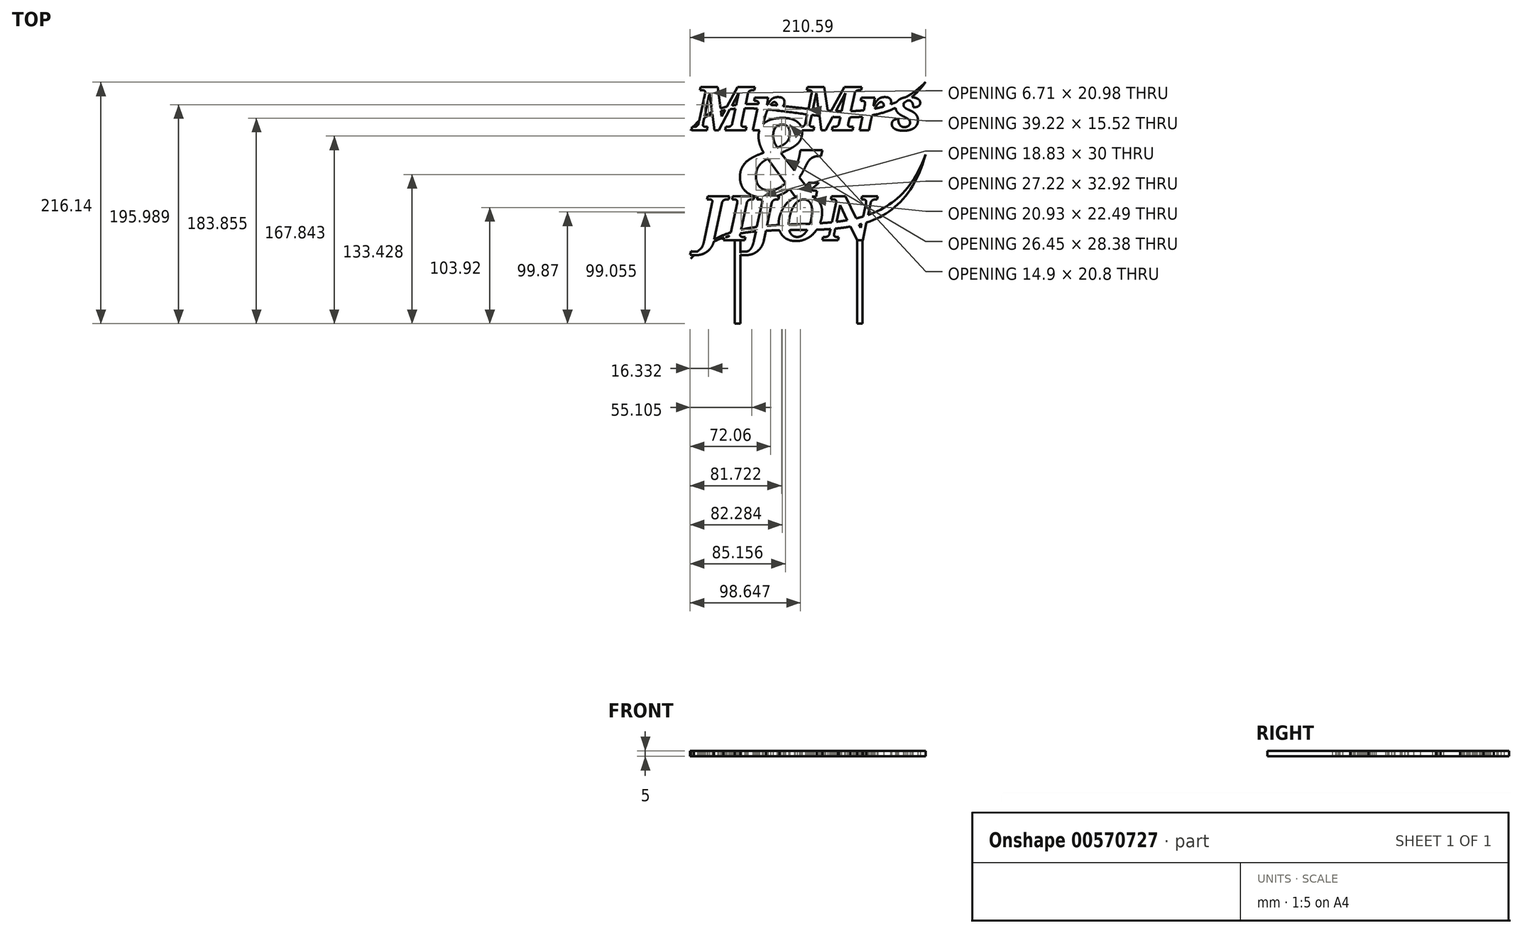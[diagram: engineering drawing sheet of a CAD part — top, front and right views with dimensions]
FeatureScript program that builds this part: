
annotation { "Feature Type Name" : "Feature", "Feature Type Description" : "" }
export const myFeature = defineFeature(function(context is Context, id is Id, definition is map)
    precondition{}
    {
        {
            var Q0;
            Q0=qCreatedBy(makeId("Top.planeOp"),FACE);
            var sketch = newSketch(context, id + "F0", { "sketchPlane" : qUnion([Q0])});
            skText(sketch, "E0", { "text": "Mr Mrs", "fontName": "NotoSerif-BoldItalic.ttf"});
            skText(sketch, "E1", { "text": "JIJÓN", "fontName": "NotoSerif-BoldItalic.ttf"});
            skText(sketch, "E2", { "text": "&", "fontName": "NotoSerif-BoldItalic.ttf"});
            skLineSegment(sketch, "E3.bottom", {"start": v(-105, -105) * mm, "end": v(105, -105) * mm, "construction": true});
            skLineSegment(sketch, "E3.top", {"start": v(-105, 105) * mm, "end": v(105, 105) * mm, "construction": true});
            skLineSegment(sketch, "E3.left", {"start": v(-105, -105) * mm, "end": v(-105, 105) * mm, "construction": true});
            skLineSegment(sketch, "E3.right", {"start": v(105, -105) * mm, "end": v(105, 105) * mm, "construction": true});
            skPoint(sketch, "E3.middle", {"position": v(0, 0) * mm});
            skPoint(sketch, "E4.1.internal.snap0", {"position": v(-96.8, -28.16) * mm});
            skFitSpline(sketch, "E5", {"points": [v(-105, -64.5) * mm, v(105, 28.69) * mm], "startDerivative": vector(161.97, 193.53) * mm, "endDerivative": vector(112.25, 314.45) * mm});
            skFitSpline(sketch, "E6", {"points": [v(-105, -64.5) * mm, v(105, 28.69) * mm], "startDerivative": vector(161.97, 179.42) * mm, "endDerivative": vector(95.19, 344.92) * mm});
            skFitSpline(sketch, "E7", {"points": [v(-105, 50.55) * mm, v(105, 93.54) * mm], "startDerivative": vector(127.56, 176.19) * mm, "endDerivative": vector(187.71, 188.88) * mm});
            skFitSpline(sketch, "E8", {"points": [v(-105, 50.55) * mm, v(105, 93.54) * mm], "startDerivative": vector(127.56, 163.36) * mm, "endDerivative": vector(158.48, 219.65) * mm});
            skLineSegment(sketch, "E9.bottom", {"start": v(-60.68, -48.16) * mm, "end": v(-65.68, -48.16) * mm});
            skLineSegment(sketch, "E9.top", {"start": v(-60.68, -122.6) * mm, "end": v(-65.68, -122.6) * mm});
            skLineSegment(sketch, "E9.left", {"start": v(-60.68, -48.16) * mm, "end": v(-60.68, -122.6) * mm});
            skLineSegment(sketch, "E9.right", {"start": v(-65.68, -48.16) * mm, "end": v(-65.68, -122.6) * mm});
            skLineSegment(sketch, "E10.bottom", {"start": v(43.74, -48.16) * mm, "end": v(48.74, -48.16) * mm});
            skLineSegment(sketch, "E10.top", {"start": v(43.74, -122.6) * mm, "end": v(48.74, -122.6) * mm});
            skLineSegment(sketch, "E10.left", {"start": v(43.74, -48.16) * mm, "end": v(43.74, -122.6) * mm});
            skLineSegment(sketch, "E10.right", {"start": v(48.74, -48.16) * mm, "end": v(48.74, -122.6) * mm});
            skPoint(sketch, "E11", {"position": v(105, 70.05) * mm});
            const initialGuessF0  = {"E0": [-0.10303, 0.05055, 1, 0, 0.039], "E1": [-0.0968, -0.04816, 1, 0, 0.04], "E2": [-0.06436, -0.00892, 1, 0, 0.07]};
            skSetInitialGuess(sketch, initialGuessF0);
            skSolve(sketch);
        }
        {
            var Q0;
            {var subQ0=sQuery(id+"F0.wireOp",EDGE,"E6");var subQ1=sQuery(id+"F0.wireOp",EDGE,"E1.sketch_text.stroke-95");var subQ2=makeQuery(id+"F0.imprint","INTERSECT",VERTEX,{"derivedFrom":[subQ1,subQ0]});var subQ3=sQuery(id+"F0.wireOp",EDGE,"E5");var subQ5=makeQuery(id+"F0.imprint","IMPRINT",EDGE,{"disambiguationData":[TD([[subQ2,1.0]])],"derivedFrom":subQ1});var subQ6=sQuery(id+"F0.wireOp",EDGE,"E1.sketch_text.stroke-115");var subQ7=makeQuery(id+"F0.imprint","INTERSECT",VERTEX,{"derivedFrom":[subQ6,subQ0]});var subQ9=makeQuery(id+"F0.imprint","IMPRINT",EDGE,{"disambiguationData":[TD([[subQ7,-1.0]])],"derivedFrom":subQ6});var subQ13=sQuery(id+"F0.wireOp",EDGE,"E1.sketch_text.stroke-37");var subQ20=makeQuery(id+"F0.imprint","IMPRINT",EDGE,{"derivedFrom":subQ13});var subQ23=sQuery(id+"F0.wireOp",EDGE,"E1.sketch_text.stroke-192");var subQ24=makeQuery(id+"F0.imprint","INTERSECT",VERTEX,{"derivedFrom":[subQ23,subQ0]});var subQ26=makeQuery(id+"F0.imprint","IMPRINT",EDGE,{"disambiguationData":[TD([[subQ24,1.0]])],"derivedFrom":subQ23});var subQ37=sQuery(id+"F0.wireOp",EDGE,"E1.sketch_text.stroke-107");var subQ40=sQuery(id+"F0.wireOp",EDGE,"E1.sketch_text.stroke-96");var subQ48=sQuery(id+"F0.wireOp",EDGE,"E0.sketch_text.stroke-152");var subQ50=sQuery(id+"F0.wireOp",EDGE,"E7");var subQ56=makeQuery(id+"F0.imprint","IMPRINT",EDGE,{"derivedFrom":subQ48});var subQ58=sQuery(id+"F0.wireOp",EDGE,"E8");var subQ59=sQuery(id+"F0.wireOp",EDGE,"E0.sketch_text.stroke-51");var subQ60=makeQuery(id+"F0.imprint","INTERSECT",VERTEX,{"derivedFrom":[subQ59,subQ58]});var subQ63=sQuery(id+"F0.wireOp",EDGE,"E0.sketch_text.stroke-24");var subQ64=sQuery(id+"F0.wireOp",EDGE,"E0.sketch_text.stroke-23");var subQ65=makeQuery(id+"F0.imprint","INTERSECT",VERTEX,{"derivedFrom":[subQ64,subQ58]});var subQ68=sQuery(id+"F0.wireOp",EDGE,"E0.sketch_text.stroke-25");var subQ75=sQuery(id+"F0.wireOp",EDGE,"E1.sketch_text.stroke-109");var subQ76=sQuery(id+"F0.wireOp",EDGE,"E1.sketch_text.stroke-108");var subQ84=sQuery(id+"F0.wireOp",EDGE,"E1.sketch_text.stroke-193");var subQ89=sQuery(id+"F0.wireOp",EDGE,"E0.sketch_text.stroke-82");var subQ106=sQuery(id+"F0.wireOp",EDGE,"E0.sketch_text.stroke-60");var subQ108=makeQuery(id+"F0.imprint","IMPRINT",EDGE,{"derivedFrom":subQ89});var subQ109=makeQuery(id+"F0.imprint","IMPRINT",EDGE,{"derivedFrom":subQ106});var subQ115=makeQuery(id+"F0.imprint","INTERSECT",VERTEX,{"derivedFrom":[subQ68,subQ50]});var subQ116=sQuery(id+"F0.wireOp",EDGE,"E0.sketch_text.stroke-26");var subQ120=sQuery(id+"F0.wireOp",EDGE,"E0.sketch_text.stroke-43");var subQ126=sQuery(id+"F0.wireOp",EDGE,"E1.sketch_text.stroke-151");var subQ127=sQuery(id+"F0.wireOp",EDGE,"E1.sketch_text.stroke-150");var subQ130=makeQuery(id+"F0.imprint","INTERSECT",VERTEX,{"derivedFrom":[subQ127,subQ3]});var subQ133=sQuery(id+"F0.wireOp",EDGE,"E1.sketch_text.stroke-168");var subQ135=sQuery(id+"F0.wireOp",EDGE,"E1.sketch_text.stroke-176");var subQ136=makeQuery(id+"F0.imprint","INTERSECT",VERTEX,{"derivedFrom":[subQ135,subQ3]});var subQ139=sQuery(id+"F0.wireOp",EDGE,"E0.sketch_text.stroke-106");var subQ140=makeQuery(id+"F0.imprint","INTERSECT",VERTEX,{"derivedFrom":[subQ139,subQ50]});var subQ142=makeQuery(id+"F0.imprint","IMPRINT",EDGE,{"disambiguationData":[TD([[subQ140,1.0]])],"derivedFrom":subQ139});var subQ143=sQuery(id+"F0.wireOp",EDGE,"E0.sketch_text.stroke-107");var subQ144=makeQuery(id+"F0.imprint","INTERSECT",VERTEX,{"derivedFrom":[subQ143,subQ58]});var subQ146=makeQuery(id+"F0.imprint","IMPRINT",EDGE,{"disambiguationData":[TD([[subQ144,1.0]])],"derivedFrom":subQ143});var subQ147=sQuery(id+"F0.wireOp",EDGE,"E0.sketch_text.stroke-136");var subQ148=sQuery(id+"F0.wireOp",EDGE,"E0.sketch_text.stroke-135");var subQ149=makeQuery(id+"F0.imprint","INTERSECT",VERTEX,{"derivedFrom":[subQ148,subQ147]});var subQ151=makeQuery(id+"F0.imprint","IMPRINT",EDGE,{"disambiguationData":[TD([[subQ149,1.0]])],"derivedFrom":subQ148});var subQ152=sQuery(id+"F0.wireOp",EDGE,"E0.sketch_text.stroke-109");var subQ153=makeQuery(id+"F0.imprint","INTERSECT",VERTEX,{"derivedFrom":[subQ152,subQ50]});var subQ155=makeQuery(id+"F0.imprint","IMPRINT",EDGE,{"disambiguationData":[TD([[subQ153,1.0]])],"derivedFrom":subQ152});var subQ161=makeQuery(id+"F0.imprint","INTERSECT",VERTEX,{"derivedFrom":[subQ116,subQ58]});var subQ162=makeQuery(id+"F0.imprint","IMPRINT",EDGE,{"disambiguationData":[TD([[subQ161,1.0]])],"derivedFrom":subQ116});var subQ166=sQuery(id+"F0.wireOp",EDGE,"E1.sketch_text.stroke-33");var subQ170=makeQuery(id+"F0.imprint","IMPRINT",EDGE,{"derivedFrom":subQ166});var subQ176=makeQuery(id+"F0.imprint","IMPRINT",EDGE,{"disambiguationData":[TD([[subQ115,1.0]])],"derivedFrom":subQ68});var subQ178=makeQuery(id+"F0.imprint","IMPRINT",EDGE,{"disambiguationData":[TD([[subQ130,1.0]])],"derivedFrom":subQ127});var subQ179=makeQuery(id+"F0.imprint","INTERSECT",VERTEX,{"derivedFrom":[subQ126,subQ0]});var subQ180=makeQuery(id+"F0.imprint","IMPRINT",EDGE,{"disambiguationData":[TD([[subQ179,1.0]])],"derivedFrom":subQ126});var subQ188=sQuery(id+"F0.wireOp",EDGE,"E0.sketch_text.stroke-183");var subQ191=sQuery(id+"F0.wireOp",EDGE,"E0.sketch_text.stroke-180");var subQ192=makeQuery(id+"F0.imprint","IMPRINT",EDGE,{"derivedFrom":subQ191});var subQ193=sQuery(id+"F0.wireOp",EDGE,"E0.sketch_text.stroke-195");var subQ195=makeQuery(id+"F0.imprint","IMPRINT",EDGE,{"derivedFrom":subQ193});var subQ199=sQuery(id+"F0.wireOp",EDGE,"E0.sketch_text.stroke-184");var subQ200=makeQuery(id+"F0.imprint","INTERSECT",VERTEX,{"derivedFrom":[subQ188,subQ199]});var subQ204=makeQuery(id+"F0.imprint","IMPRINT",EDGE,{"disambiguationData":[TD([[subQ200,1.0]])],"derivedFrom":subQ188});var subQ208=sQuery(id+"F0.wireOp",EDGE,"E0.sketch_text.stroke-27");var subQ209=sQuery(id+"F0.wireOp",EDGE,"E0.sketch_text.stroke-36");var subQ212=sQuery(id+"F0.wireOp",EDGE,"E0.sketch_text.stroke-38");var subQ221=sQuery(id+"F0.wireOp",EDGE,"E0.sketch_text.stroke-68");var subQ222=makeQuery(id+"F0.imprint","IMPRINT",EDGE,{"derivedFrom":subQ221});var subQ228=makeQuery(id+"F0.imprint","IMPRINT",EDGE,{"disambiguationData":[TD([[subQ136,-1.0]])],"derivedFrom":subQ135});var subQ229=sQuery(id+"F0.wireOp",EDGE,"E1.sketch_text.stroke-177");var subQ230=makeQuery(id+"F0.imprint","INTERSECT",VERTEX,{"derivedFrom":[subQ229,subQ3]});var subQ232=makeQuery(id+"F0.imprint","IMPRINT",EDGE,{"disambiguationData":[TD([[subQ230,1.0]])],"derivedFrom":subQ229});var subQ233=sQuery(id+"F0.wireOp",EDGE,"E0.sketch_text.stroke-6");var subQ235=makeQuery(id+"F0.imprint","INTERSECT",VERTEX,{"derivedFrom":[subQ233,subQ58]});var subQ236=makeQuery(id+"F0.imprint","IMPRINT",EDGE,{"disambiguationData":[TD([[subQ235,1.0]])],"derivedFrom":subQ233});var subQ237=sQuery(id+"F0.wireOp",EDGE,"E1.sketch_text.stroke-12");var subQ238=makeQuery(id+"F0.imprint","IMPRINT",EDGE,{"derivedFrom":subQ237});var subQ239=sQuery(id+"F0.wireOp",EDGE,"E1.sketch_text.stroke-4");var subQ244=makeQuery(id+"F0.imprint","INTERSECT",VERTEX,{"derivedFrom":[subQ239,subQ0]});var subQ245=makeQuery(id+"F0.imprint","IMPRINT",EDGE,{"disambiguationData":[TD([[subQ244,-1.0]])],"derivedFrom":subQ239});var subQ259=sQuery(id+"F0.wireOp",EDGE,"E1.sketch_text.stroke-48");var subQ260=sQuery(id+"F0.wireOp",EDGE,"E1.sketch_text.stroke-47");var subQ261=makeQuery(id+"F0.imprint","INTERSECT",VERTEX,{"derivedFrom":[subQ260,subQ259]});var subQ264=makeQuery(id+"F0.imprint","IMPRINT",EDGE,{"disambiguationData":[TD([[subQ261,1.0]])],"derivedFrom":subQ260});var subQ268=makeQuery(id+"F0.imprint","INTERSECT",VERTEX,{"derivedFrom":[subQ212,subQ50]});var subQ269=makeQuery(id+"F0.imprint","IMPRINT",EDGE,{"disambiguationData":[TD([[subQ268,-1.0]])],"derivedFrom":subQ212});var subQ270=sQuery(id+"F0.wireOp",EDGE,"E0.sketch_text.stroke-22");var subQ271=makeQuery(id+"F0.imprint","INTERSECT",VERTEX,{"derivedFrom":[subQ270,subQ50]});var subQ273=makeQuery(id+"F0.imprint","IMPRINT",EDGE,{"disambiguationData":[TD([[subQ271,1.0]])],"derivedFrom":subQ270});var subQ276=sQuery(id+"F0.wireOp",EDGE,"E1.sketch_text.stroke-79");var subQ277=makeQuery(id+"F0.imprint","INTERSECT",VERTEX,{"derivedFrom":[subQ276,subQ3]});var subQ302=sQuery(id+"F0.wireOp",EDGE,"E0.sketch_text.stroke-79");var subQ305=sQuery(id+"F0.wireOp",EDGE,"E0.sketch_text.stroke-120");var subQ309=sQuery(id+"F0.wireOp",EDGE,"E1.sketch_text.stroke-102");var subQ310=makeQuery(id+"F0.imprint","IMPRINT",EDGE,{"derivedFrom":subQ309});var subQ311=sQuery(id+"F0.wireOp",EDGE,"E2.sketch_text.stroke-14");var subQ312=makeQuery(id+"F0.imprint","INTERSECT",VERTEX,{"derivedFrom":[subQ302,subQ311]});var subQ313=makeQuery(id+"F0.imprint","IMPRINT",EDGE,{"disambiguationData":[TD([[subQ312,-1.0]])],"derivedFrom":subQ302});var subQ315=makeQuery(id+"F0.imprint","IMPRINT",EDGE,{"derivedFrom":sQuery(id+"F0.wireOp",EDGE,"E1.sketch_text.stroke-136")});var subQ319=makeQuery(id+"F0.imprint","IMPRINT",EDGE,{"derivedFrom":subQ305});var subQ336=sQuery(id+"F0.wireOp",EDGE,"E1.sketch_text.stroke-70");var subQ337=sQuery(id+"F0.wireOp",EDGE,"E1.sketch_text.stroke-69");var subQ338=makeQuery(id+"F0.imprint","INTERSECT",VERTEX,{"derivedFrom":[subQ337,subQ336]});var subQ341=makeQuery(id+"F0.imprint","IMPRINT",EDGE,{"disambiguationData":[TD([[subQ338,1.0]])],"derivedFrom":subQ337});var subQ345=makeQuery(id+"F0.imprint","IMPRINT",EDGE,{"disambiguationData":[TD([[subQ60,1.0]])],"derivedFrom":subQ59});var subQ350=sQuery(id+"F0.wireOp",EDGE,"E0.sketch_text.stroke-62");var subQ353=sQuery(id+"F0.wireOp",EDGE,"E0.sketch_text.stroke-185");var subQ355=sQuery(id+"F0.wireOp",EDGE,"E0.sketch_text.stroke-182");var subQ359=sQuery(id+"F0.wireOp",EDGE,"E0.sketch_text.stroke-162");var subQ360=sQuery(id+"F0.wireOp",EDGE,"E0.sketch_text.stroke-161");var subQ365=sQuery(id+"F0.wireOp",EDGE,"E0.sketch_text.stroke-108");var subQ368=sQuery(id+"F0.wireOp",EDGE,"E1.sketch_text.stroke-64");var subQ373=sQuery(id+"F0.wireOp",EDGE,"E1.sketch_text.stroke-35");var subQ379=sQuery(id+"F0.wireOp",EDGE,"E0.sketch_text.stroke-91");var subQ380=sQuery(id+"F0.wireOp",EDGE,"E0.sketch_text.stroke-90");var subQ384=sQuery(id+"F0.wireOp",EDGE,"E0.sketch_text.stroke-54");var subQ386=makeQuery(id+"F0.imprint","INTERSECT",VERTEX,{"derivedFrom":[subQ209,subQ50]});var subQ387=makeQuery(id+"F0.imprint","IMPRINT",EDGE,{"disambiguationData":[TD([[subQ386,1.0]])],"derivedFrom":subQ209});var subQ389=sQuery(id+"F0.wireOp",EDGE,"E0.sketch_text.stroke-37");var subQ391=sQuery(id+"F0.wireOp",EDGE,"E0.sketch_text.stroke-7");var subQ396=makeQuery(id+"F0.imprint","INTERSECT",VERTEX,{"derivedFrom":[subQ127,subQ84]});var subQ400=sQuery(id+"F0.wireOp",EDGE,"E0.sketch_text.stroke-110");var subQ404=sQuery(id+"F0.wireOp",EDGE,"E0.sketch_text.stroke-127");var subQ412=makeQuery(id+"F0.imprint","INTERSECT",VERTEX,{"derivedFrom":[subQ400,subQ58]});var subQ413=makeQuery(id+"F0.imprint","IMPRINT",EDGE,{"disambiguationData":[TD([[subQ412,1.0]])],"derivedFrom":subQ400});var subQ414=sQuery(id+"F0.wireOp",EDGE,"E1.sketch_text.stroke-5");var subQ417=sQuery(id+"F0.wireOp",EDGE,"E1.sketch_text.stroke-1");var subQ421=makeQuery(id+"F0.imprint","INTERSECT",VERTEX,{"derivedFrom":[subQ380,subQ50]});var subQ422=makeQuery(id+"F0.imprint","IMPRINT",EDGE,{"disambiguationData":[TD([[subQ421,-1.0]])],"derivedFrom":subQ380});var subQ428=sQuery(id+"F0.wireOp",EDGE,"E0.sketch_text.stroke-111");var subQ436=sQuery(id+"F0.wireOp",EDGE,"E0.sketch_text.stroke-160");var subQ442=sQuery(id+"F0.wireOp",EDGE,"E1.sketch_text.stroke-14");var subQ445=makeQuery(id+"F0.imprint","INTERSECT",VERTEX,{"derivedFrom":[subQ37,subQ76]});var subQ447=makeQuery(id+"F0.imprint","IMPRINT",EDGE,{"disambiguationData":[TD([[subQ445,1.0]])],"derivedFrom":subQ37});var subQ455=sQuery(id+"F0.wireOp",EDGE,"E1.sketch_text.stroke-39");var subQ459=sQuery(id+"F0.wireOp",EDGE,"E0.sketch_text.stroke-77");var subQ461=makeQuery(id+"F0.imprint","INTERSECT",VERTEX,{"derivedFrom":[subQ436,subQ360]});var subQ462=makeQuery(id+"F0.imprint","IMPRINT",EDGE,{"disambiguationData":[TD([[subQ461,1.0]])],"derivedFrom":subQ436});var subQ464=makeQuery(id+"F0.imprint","IMPRINT",EDGE,{"disambiguationData":[TD([[subQ65,1.0]])],"derivedFrom":subQ64});var subQ465=sQuery(id+"F0.wireOp",EDGE,"E1.sketch_text.stroke-139");var subQ467=sQuery(id+"F0.wireOp",EDGE,"E9.top");var subQ471=sQuery(id+"F0.wireOp",EDGE,"E1.sketch_text.stroke-152");var subQ473=sQuery(id+"F0.wireOp",EDGE,"E1.sketch_text.stroke-178");Q0=qUnion([makeQuery(id+"F0.imprint","IMPRINT",FACE,{"disambiguationData":[TD([[makeQuery(id+"F0.imprint","IMPRINT",EDGE,{"derivedFrom":subQ473}),-1.0]])]}),makeQuery(id+"F0.imprint","IMPRINT",FACE,{"disambiguationData":[TD([[makeQuery(id+"F0.imprint","IMPRINT",EDGE,{"derivedFrom":subQ471}),-1.0]])]}),makeQuery(id+"F0.imprint","IMPRINT",FACE,{"disambiguationData":[TD([[subQ176,-1.0]])]}),makeQuery(id+"F0.imprint","IMPRINT",FACE,{"disambiguationData":[TD([[subQ462,-1.0]])]}),makeQuery(id+"F0.imprint","IMPRINT",FACE,{"disambiguationData":[TD([[makeQuery(id+"F0.imprint","IMPRINT",EDGE,{"derivedFrom":sQuery(id+"F0.wireOp",EDGE,"E0.sketch_text.stroke-84")}),-1.0]])]}),makeQuery(id+"F0.imprint","IMPRINT",FACE,{"disambiguationData":[TD([[makeQuery(id+"F0.imprint","IMPRINT",EDGE,{"derivedFrom":subQ467}),-1.0]])]}),makeQuery(id+"F0.imprint","IMPRINT",FACE,{"disambiguationData":[TD([[subQ447,1.0]])]}),makeQuery(id+"F0.imprint","IMPRINT",FACE,{"disambiguationData":[TD([[subQ273,1.0]])]}),makeQuery(id+"F0.imprint","IMPRINT",FACE,{"disambiguationData":[TD([[subQ319,-1.0]])]}),makeQuery(id+"F0.imprint","IMPRINT",FACE,{"disambiguationData":[TD([[makeQuery(id+"F0.imprint","IMPRINT",EDGE,{"derivedFrom":subQ465}),-1.0]])]}),makeQuery(id+"F0.imprint","IMPRINT",FACE,{"disambiguationData":[TD([[subQ464,-1.0]])]}),makeQuery(id+"F0.imprint","IMPRINT",FACE,{"disambiguationData":[TD([[subQ56,1.0]])]}),makeQuery(id+"F0.imprint","IMPRINT",FACE,{"disambiguationData":[TD([[makeQuery(id+"F0.imprint","IMPRINT",EDGE,{"derivedFrom":subQ459}),-1.0]])]}),makeQuery(id+"F0.imprint","IMPRINT",FACE,{"disambiguationData":[TD([[makeQuery(id+"F0.imprint","IMPRINT",EDGE,{"derivedFrom":subQ455}),-1.0]])]}),makeQuery(id+"F0.imprint","IMPRINT",FACE,{"disambiguationData":[TD([[subQ310,-1.0]])]}),makeQuery(id+"F0.imprint","IMPRINT",FACE,{"disambiguationData":[TD([[makeQuery(id+"F0.imprint","IMPRINT",EDGE,{"derivedFrom":sQuery(id+"F0.wireOp",EDGE,"E0.sketch_text.stroke-0")}),-1.0]])]}),makeQuery(id+"F0.imprint","IMPRINT",FACE,{"disambiguationData":[TD([[subQ245,1.0]])]}),makeQuery(id+"F0.imprint","IMPRINT",FACE,{"disambiguationData":[TD([[subQ447,-1.0]])]}),makeQuery(id+"F0.imprint","IMPRINT",FACE,{"disambiguationData":[TD([[subQ222,1.0]])]}),makeQuery(id+"F0.imprint","IMPRINT",FACE,{"disambiguationData":[TD([[makeQuery(id+"F0.imprint","IMPRINT",EDGE,{"derivedFrom":subQ442}),-1.0]])]}),makeQuery(id+"F0.imprint","IMPRINT",FACE,{"disambiguationData":[TD([[subQ413,-1.0]])]}),makeQuery(id+"F0.imprint","IMPRINT",FACE,{"disambiguationData":[TD([[makeQuery(id+"F0.imprint","IMPRINT",EDGE,{"derivedFrom":sQuery(id+"F0.wireOp",EDGE,"E0.sketch_text.stroke-138")}),-1.0]])]}),makeQuery(id+"F0.imprint","IMPRINT",FACE,{"disambiguationData":[TD([[subQ232,-1.0]])]}),makeQuery(id+"F0.imprint","IMPRINT",FACE,{"disambiguationData":[TD([[subQ195,1.0]])]}),makeQuery(id+"F0.imprint","IMPRINT",FACE,{"disambiguationData":[TD([[subQ238,1.0]])]}),makeQuery(id+"F0.imprint","IMPRINT",FACE,{"disambiguationData":[TD([[subQ422,-1.0]])]}),makeQuery(id+"F0.imprint","IMPRINT",FACE,{"disambiguationData":[TD([[makeQuery(id+"F0.imprint","IMPRINT",EDGE,{"derivedFrom":subQ428}),-1.0]])]}),makeQuery(id+"F0.imprint","IMPRINT",FACE,{"disambiguationData":[TD([[subQ422,1.0]])]}),makeQuery(id+"F0.imprint","IMPRINT",FACE,{"disambiguationData":[TD([[subQ180,-1.0]])]}),makeQuery(id+"F0.imprint","IMPRINT",FACE,{"disambiguationData":[TD([[makeQuery(id+"F0.imprint","IMPRINT",EDGE,{"derivedFrom":subQ417}),-1.0]])]}),makeQuery(id+"F0.imprint","IMPRINT",FACE,{"disambiguationData":[TD([[makeQuery(id+"F0.imprint","IMPRINT",EDGE,{"derivedFrom":subQ414}),-1.0]])]}),makeQuery(id+"F0.imprint","IMPRINT",FACE,{"disambiguationData":[TD([[subQ155,1.0]])]}),makeQuery(id+"F0.imprint","IMPRINT",FACE,{"disambiguationData":[TD([[subQ315,-1.0]])]}),makeQuery(id+"F0.imprint","IMPRINT",FACE,{"disambiguationData":[TD([[subQ313,-1.0]])]}),makeQuery(id+"F0.imprint","IMPRINT",FACE,{"disambiguationData":[TD([[subQ178,-1.0]])]}),makeQuery(id+"F0.imprint","IMPRINT",FACE,{"disambiguationData":[TD([[subQ387,-1.0]])]}),makeQuery(id+"F0.imprint","IMPRINT",FACE,{"disambiguationData":[TD([[makeQuery(id+"F0.imprint","IMPRINT",EDGE,{"derivedFrom":subQ404}),-1.0]])]}),makeQuery(id+"F0.imprint","IMPRINT",FACE,{"disambiguationData":[TD([[makeQuery(id+"F0.imprint","IMPRINT",EDGE,{"disambiguationData":[TD([[subQ396,-1.0]])],"derivedFrom":subQ127}),-1.0]])]}),makeQuery(id+"F0.imprint","IMPRINT",FACE,{"disambiguationData":[TD([[makeQuery(id+"F0.imprint","IMPRINT",EDGE,{"derivedFrom":subQ391}),-1.0]])]}),makeQuery(id+"F0.imprint","IMPRINT",FACE,{"disambiguationData":[TD([[makeQuery(id+"F0.imprint","IMPRINT",EDGE,{"derivedFrom":subQ389}),-1.0]])]}),makeQuery(id+"F0.imprint","IMPRINT",FACE,{"disambiguationData":[TD([[subQ387,1.0]])]}),makeQuery(id+"F0.imprint","IMPRINT",FACE,{"disambiguationData":[TD([[makeQuery(id+"F0.imprint","IMPRINT",EDGE,{"derivedFrom":subQ384}),-1.0]])]}),makeQuery(id+"F0.imprint","IMPRINT",FACE,{"disambiguationData":[TD([[subQ109,1.0]])]}),makeQuery(id+"F0.imprint","IMPRINT",FACE,{"disambiguationData":[TD([[makeQuery(id+"F0.imprint","IMPRINT",EDGE,{"derivedFrom":subQ379}),-1.0]])]}),makeQuery(id+"F0.imprint","IMPRINT",FACE,{"disambiguationData":[TD([[makeQuery(id+"F0.imprint","IMPRINT",EDGE,{"derivedFrom":subQ373}),-1.0]])]}),makeQuery(id+"F0.imprint","IMPRINT",FACE,{"disambiguationData":[TD([[subQ170,1.0]])]}),makeQuery(id+"F0.imprint","IMPRINT",FACE,{"disambiguationData":[TD([[makeQuery(id+"F0.imprint","IMPRINT",EDGE,{"derivedFrom":subQ368}),-1.0]])]}),makeQuery(id+"F0.imprint","IMPRINT",FACE,{"disambiguationData":[TD([[makeQuery(id+"F0.imprint","IMPRINT",EDGE,{"derivedFrom":subQ365}),-1.0]])]}),makeQuery(id+"F0.imprint","IMPRINT",FACE,{"disambiguationData":[TD([[subQ151,1.0]])]}),makeQuery(id+"F0.imprint","IMPRINT",FACE,{"disambiguationData":[TD([[makeQuery(id+"F0.imprint","IMPRINT",EDGE,{"derivedFrom":subQ359}),-1.0]])]}),makeQuery(id+"F0.imprint","IMPRINT",FACE,{"disambiguationData":[TD([[makeQuery(id+"F0.imprint","IMPRINT",EDGE,{"derivedFrom":sQuery(id+"F0.wireOp",EDGE,"E0.sketch_text.stroke-168")}),-1.0]])]}),makeQuery(id+"F0.imprint","IMPRINT",FACE,{"disambiguationData":[TD([[makeQuery(id+"F0.imprint","IMPRINT",EDGE,{"derivedFrom":subQ355}),-1.0]])]}),makeQuery(id+"F0.imprint","IMPRINT",FACE,{"disambiguationData":[TD([[subQ204,1.0]])]}),makeQuery(id+"F0.imprint","IMPRINT",FACE,{"disambiguationData":[TD([[makeQuery(id+"F0.imprint","IMPRINT",EDGE,{"derivedFrom":subQ353}),-1.0]])]}),makeQuery(id+"F0.imprint","IMPRINT",FACE,{"disambiguationData":[TD([[makeQuery(id+"F0.imprint","IMPRINT",EDGE,{"derivedFrom":subQ350}),-1.0]])]}),makeQuery(id+"F0.imprint","IMPRINT",FACE,{"disambiguationData":[TD([[subQ345,1.0]])]}),makeQuery(id+"F0.imprint","IMPRINT",FACE,{"disambiguationData":[TD([[subQ341,-1.0]])]}),makeQuery(id+"F0.imprint","IMPRINT",FACE,{"disambiguationData":[TD([[subQ319,1.0]])]}),makeQuery(id+"F0.imprint","IMPRINT",FACE,{"disambiguationData":[TD([[makeQuery(id+"F0.imprint","IMPRINT",EDGE,{"disambiguationData":[TD([[subQ277,1.0]])],"derivedFrom":subQ276}),-1.0]])]}),makeQuery(id+"F0.imprint","IMPRINT",FACE,{"disambiguationData":[TD([[subQ236,-1.0]])]}),makeQuery(id+"F0.imprint","IMPRINT",FACE,{"disambiguationData":[TD([[subQ269,1.0]])]}),makeQuery(id+"F0.imprint","IMPRINT",FACE,{"disambiguationData":[TD([[subQ264,-1.0]])]}),makeQuery(id+"F0.imprint","IMPRINT",FACE,{"disambiguationData":[TD([[subQ238,-1.0]])]}),makeQuery(id+"F0.imprint","IMPRINT",FACE,{"disambiguationData":[TD([[subQ108,1.0]])]}),makeQuery(id+"F0.imprint","IMPRINT",FACE,{"disambiguationData":[TD([[subQ228,1.0]])]}),makeQuery(id+"F0.imprint","IMPRINT",FACE,{"disambiguationData":[TD([[subQ222,-1.0]])]}),makeQuery(id+"F0.imprint","IMPRINT",FACE,{"disambiguationData":[TD([[makeQuery(id+"F0.imprint","IMPRINT",EDGE,{"derivedFrom":subQ208}),-1.0]])]}),makeQuery(id+"F0.imprint","IMPRINT",FACE,{"disambiguationData":[TD([[subQ192,-1.0]])]}),makeQuery(id+"F0.imprint","IMPRINT",FACE,{"disambiguationData":[TD([[subQ178,1.0]])]}),makeQuery(id+"F0.imprint","IMPRINT",FACE,{"disambiguationData":[TD([[subQ176,1.0]])]}),makeQuery(id+"F0.imprint","IMPRINT",FACE,{"disambiguationData":[TD([[subQ9,-1.0]])]}),makeQuery(id+"F0.imprint","IMPRINT",FACE,{"disambiguationData":[TD([[subQ170,-1.0]])]}),makeQuery(id+"F0.imprint","IMPRINT",FACE,{"disambiguationData":[TD([[subQ162,-1.0]])]}),makeQuery(id+"F0.imprint","IMPRINT",FACE,{"disambiguationData":[TD([[subQ146,-1.0]])]}),makeQuery(id+"F0.imprint","IMPRINT",FACE,{"disambiguationData":[TD([[subQ142,1.0]])]}),makeQuery(id+"F0.imprint","IMPRINT",FACE,{"disambiguationData":[TD([[makeQuery(id+"F0.imprint","IMPRINT",EDGE,{"derivedFrom":subQ133}),-1.0]])]}),makeQuery(id+"F0.imprint","IMPRINT",FACE,{"disambiguationData":[TD([[makeQuery(id+"F0.imprint","IMPRINT",EDGE,{"derivedFrom":subQ120}),-1.0]])]}),makeQuery(id+"F0.imprint","IMPRINT",FACE,{"disambiguationData":[TD([[subQ109,-1.0]])]}),makeQuery(id+"F0.imprint","IMPRINT",FACE,{"disambiguationData":[TD([[makeQuery(id+"F0.imprint","IMPRINT",EDGE,{"derivedFrom":sQuery(id+"F0.wireOp",EDGE,"E10.top")}),1.0]])]}),makeQuery(id+"F0.imprint","IMPRINT",FACE,{"disambiguationData":[TD([[makeQuery(id+"F0.imprint","IMPRINT",EDGE,{"derivedFrom":subQ75}),-1.0]])]}),makeQuery(id+"F0.imprint","IMPRINT",FACE,{"disambiguationData":[TD([[makeQuery(id+"F0.imprint","IMPRINT",EDGE,{"derivedFrom":subQ63}),-1.0]])]}),makeQuery(id+"F0.imprint","IMPRINT",FACE,{"disambiguationData":[TD([[subQ56,-1.0]])]}),makeQuery(id+"F0.imprint","IMPRINT",FACE,{"disambiguationData":[TD([[makeQuery(id+"F0.imprint","IMPRINT",EDGE,{"derivedFrom":subQ40}),-1.0]])]}),makeQuery(id+"F0.imprint","IMPRINT",FACE,{"disambiguationData":[TD([[subQ26,1.0]])]}),makeQuery(id+"F0.imprint","IMPRINT",FACE,{"disambiguationData":[TD([[subQ20,-1.0]])]}),makeQuery(id+"F0.imprint","IMPRINT",FACE,{"disambiguationData":[TD([[subQ5,1.0]])]})]);}
            var Q1;
            {var subQ12=sQuery(id+"F0.wireOp",EDGE,"E1.sketch_text.stroke-80");Q1=makeQuery(id+"F0.imprint","IMPRINT",FACE,{"disambiguationData":[TD([[makeQuery(id+"F0.imprint","IMPRINT",EDGE,{"derivedFrom":subQ12}),-1.0]])]});}
            var Q2;
            {var subQ0=sQuery(id+"F0.wireOp",EDGE,"E1.sketch_text.stroke-88");var subQ1=sQuery(id+"F0.wireOp",EDGE,"E1.sketch_text.stroke-87");var subQ2=makeQuery(id+"F0.imprint","INTERSECT",VERTEX,{"derivedFrom":[subQ1,subQ0]});Q2=makeQuery(id+"F0.imprint","IMPRINT",FACE,{"disambiguationData":[TD([[makeQuery(id+"F0.imprint","IMPRINT",EDGE,{"disambiguationData":[TD([[subQ2,1.0]])],"derivedFrom":subQ1}),-1.0]])]});}
            var Q3;
            {var subQ5=sQuery(id+"F0.wireOp",EDGE,"E1.sketch_text.stroke-135");var subQ6=sQuery(id+"F0.wireOp",EDGE,"E1.sketch_text.stroke-116");var subQ7=makeQuery(id+"F0.imprint","INTERSECT",VERTEX,{"derivedFrom":[subQ6,subQ5]});Q3=makeQuery(id+"F0.imprint","IMPRINT",FACE,{"disambiguationData":[TD([[makeQuery(id+"F0.imprint","IMPRINT",EDGE,{"disambiguationData":[TD([[subQ7,-1.0]])],"derivedFrom":subQ6}),1.0]])]});}
            var Q4;
            {var subQ0=sQuery(id+"F0.wireOp",EDGE,"E5");var subQ1=sQuery(id+"F0.wireOp",EDGE,"E1.sketch_text.stroke-54");var subQ2=makeQuery(id+"F0.imprint","INTERSECT",VERTEX,{"derivedFrom":[subQ1,subQ0]});Q4=makeQuery(id+"F0.imprint","IMPRINT",FACE,{"disambiguationData":[TD([[makeQuery(id+"F0.imprint","IMPRINT",EDGE,{"disambiguationData":[TD([[subQ2,-1.0]])],"derivedFrom":subQ1}),1.0]])]});}
            extrude(context, id + "F1", {"entities" : qUnion([Q0, Q1, Q2, Q3, Q4]), "depth" : 5 * mm, "offsetDistance" : 25 * mm});
        }
    });
